# Revit family: 207_69e8cd24fe9145a2b212c1c89e297a
name_source: partatom
category: Air Terminals
units: mm (PartAtom-declared; Revit-internal decimal feet)

## family parameters
Always vertical = Yes
Cut with Voids When Loaded = No
Part Type = Normal
Room Calculation Point = Yes
Round Connector Dimension = Use Diameter
Shared = No
Work Plane-Based = No

## types (1)
- VILPE 160S
    CAT0 = Yes
    CLBTZ = 0 mm  [stored 0 ft]
    CL_Location_5000 = 5000 mm  [stored 16.4042 ft]
    D = 160 mm
    D12 = 155 mm  [stored 0.50853 ft]
    DR = 118 mm
    Description = Intake vent
    H1 = 343 mm  [stored 1.12533 ft]
    H2 = 54 mm  [stored 0.177165 ft]
    H_ARR = 0 mm  [stored 0 ft]
    L = 300 mm  [stored 0.984252 ft]
    L_ARR = 400 mm  [stored 1.31234 ft]
    MC Product Code = VILPE 160S
    Manufacturer = Vilpe
    QmdConnectorList = 201;D
    W_ARR = 400 mm  [stored 1.31234 ft]
    XRefLineVPlnId = 7453
    YRefLineVPlnId = 7456
    Z1 = 26 mm
    Z2 = 29 mm
    magiPartTypeId = 207
    magiProductFamilyId = 69e8cd24fe9145a2b212c1c89e297a
    magiProductId = d8c904476cfc44cc8439c3615aa86b

note: [stored X ft] marks values corroborated as IEEE doubles in the binary element streams (Revit-internal decimal feet)

## geometry (parser evidence)
native form markers: Sweep x1
no freeform markers — native parametric forms only
